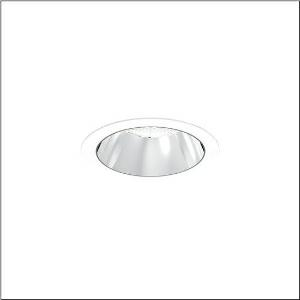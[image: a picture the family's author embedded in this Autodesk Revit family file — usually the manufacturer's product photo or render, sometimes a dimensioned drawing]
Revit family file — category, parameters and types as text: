
# Revit family: lunis_21_l_51db15ed91c
name_source: partatom
category: Lighting Fixtures
units: mm (PartAtom-declared; Revit-internal decimal feet)

## family parameters
Cut with Voids When Loaded = No
Host = Face
Light Source = No
Part Type = Normal
Room Calculation Point = No
Round Connector Dimension = Use Diameter
Shared = No

## types (1)
- --- (1 x LED, 4060 lm, 25.4 W, 6500K)
    Apparent Load = 25 VA
    CIE Flux Codes = 93 100 100 100 100
    Color Rendering = 80
    Color Temperature = 6500K
    Default Elevation = 1800 mm
    Description = Lunis 21,  L, downlight, light control with lens, of PMMA, anti glare with reflector, of PC, highly specular, light emission: direct distribution, LED rated luminous flux: 2.120lm, light colour: 830/840/865, with terminal, 5-pole, mains connection: 220..240V, AC/DC, 0/50..60Hz, housing, round, of diecast aluminium, traffic white (RAL 9016), diameter: 165mm, clamping range: 1..40mm, protection rating (complete): IP20, protection rating (on room side): IP54, insulation class (complete): insulation class II (safety insulation), certification: CE, impact resistance: IK03, packaging unit: 1 piece
    Height = 0 mm  [stored 0 ft]
    Lamp = 1 x LED
    Lamp Light Flux = 4060 lm
    Lamp Power = 25.4 W
    Lamp count = 1
    Length = 165 mm
    Luminous efficacy = 160 lm/W
    Manufacturer = Siteco
    ModVariant = No
    Model = 51DB15ED91C
    Mounting Place = Ceiling
    Mounting Type = Recessed
    Number of Poles = 1
    OnlyDefault = Yes
    Power Factor = 1
    Product Name = Lunis 21 L
    Product group = downlight
    ProductGroupID = 400
    Protection Class = Protection class II
    Protection Degree = IP 20
    RLX_Detail_Level = 1
    RLX_Emergency_Light_Flux = 0 lm
    RLX_Emergency_Type = 0
    RLX_Emergency_Type_DB = No
    RlxData = <blob elided: 18237 chars, md5=ca698d4e>
    Socket = socket
    Standby Power = 0 W
    System Light Flux = 4060 lm
    System Power = 25 W
    Type Comments = individual setting: colour temperature 6500K, luminous flux: 100 % | (ON | ON | OFF | OFF) | 700 mA
    Type Image = l_1291167.jpg
    URL = http://relux.com
    VarID = @adj_020418
    Voltage = 0 V
    Weight = 0.00 kg
    Width = 0 mm  [stored 0 ft]

note: [stored X ft] marks values corroborated as IEEE doubles in the binary element streams (Revit-internal decimal feet)

## geometry (parser evidence)
native form markers: Blend x4, Sweep x10
no freeform markers — native parametric forms only
